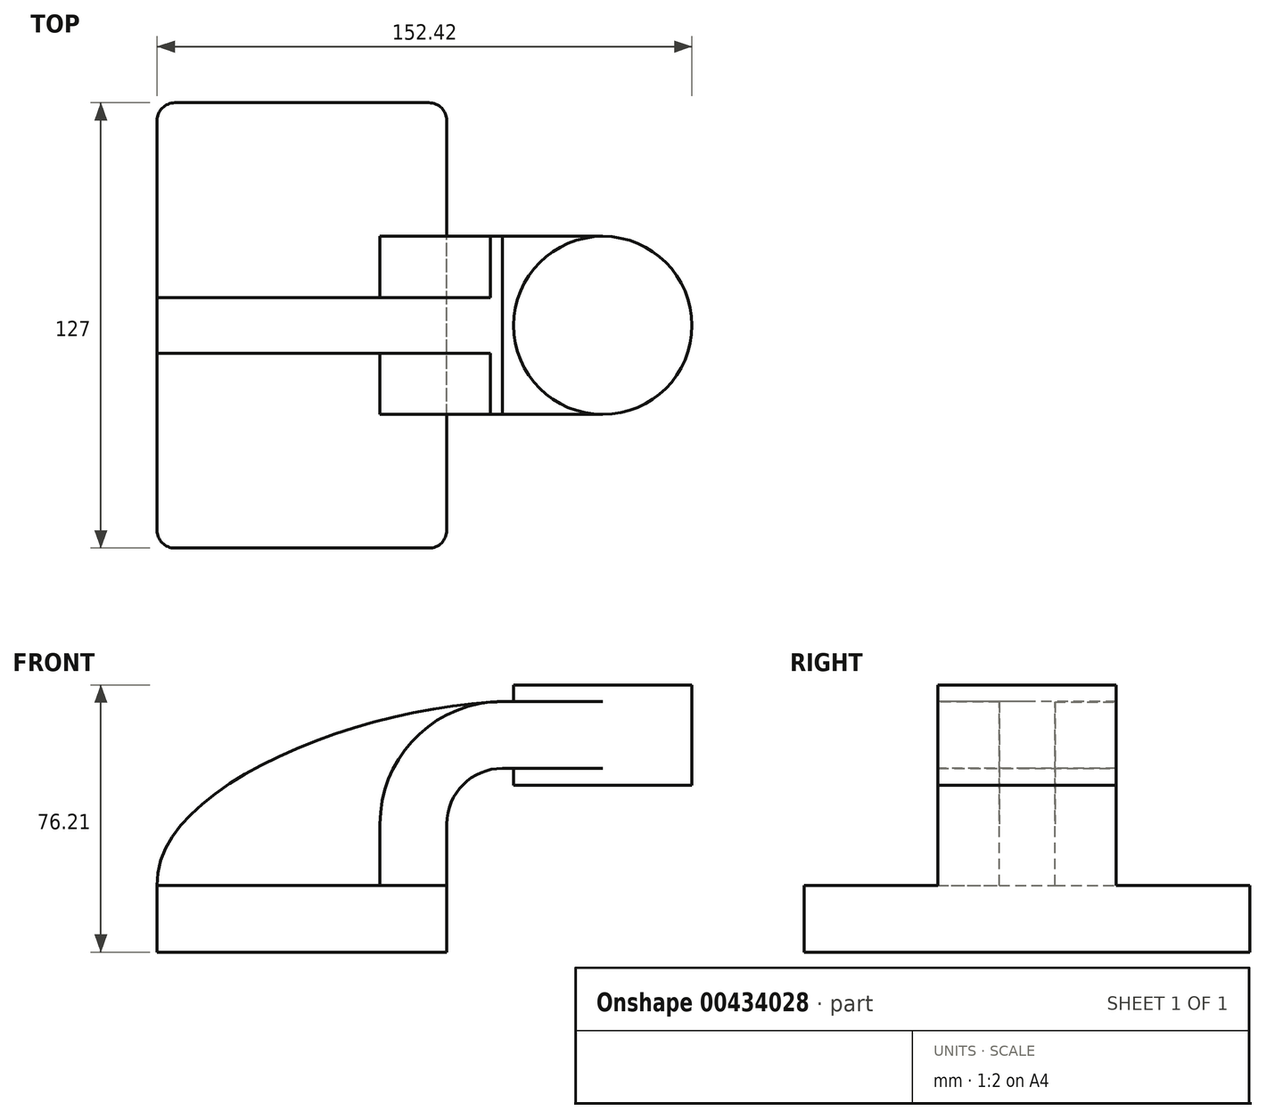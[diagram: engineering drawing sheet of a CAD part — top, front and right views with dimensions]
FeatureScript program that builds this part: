
annotation { "Feature Type Name" : "Feature", "Feature Type Description" : "" }
export const myFeature = defineFeature(function(context is Context, id is Id, definition is map)
    precondition{}
    {
        {
            var Q0;
            Q0=qCreatedBy(makeId("Front.planeOp"),FACE);
            var sketch = newSketch(context, id + "F0", { "sketchPlane" : qUnion([Q0])});
            skLineSegment(sketch, "E0.rect.bottom", {"start": v(-41.28, 9.52) * mm, "end": v(41.28, 9.52) * mm});
            skLineSegment(sketch, "E0.rect.top", {"start": v(-41.28, -9.52) * mm, "end": v(41.28, -9.52) * mm});
            skLineSegment(sketch, "E0.rect.left", {"start": v(-41.28, 9.52) * mm, "end": v(-41.28, -9.52) * mm});
            skLineSegment(sketch, "E0.rect.right", {"start": v(41.28, 9.52) * mm, "end": v(41.28, -9.52) * mm});
            skPoint(sketch, "E0.rect.middle", {"position": v(0, 0) * mm});
            skLineSegment(sketch, "E1", {"start": v(41.28, 9.52) * mm, "end": v(41.28, 27) * mm});
            skArc(sketch, "E2", {"start": v(41.28, 27) * mm, "mid": v(45.92, 38.23) * mm, "end": v(57.15, 42.88) * mm});
            skLineSegment(sketch, "E3", {"start": v(57.15, 42.88) * mm, "end": v(85.72, 42.88) * mm});
            skLineSegment(sketch, "E4.rect.bottom", {"start": v(60.32, 38.1) * mm, "end": v(111.12, 38.1) * mm});
            skLineSegment(sketch, "E4.rect.top", {"start": v(60.32, 66.68) * mm, "end": v(111.12, 66.68) * mm});
            skLineSegment(sketch, "E4.rect.left", {"start": v(60.32, 38.1) * mm, "end": v(60.32, 66.68) * mm});
            skLineSegment(sketch, "E4.rect.right", {"start": v(111.13, 38.1) * mm, "end": v(111.12, 66.68) * mm});
            skPoint(sketch, "E4.rect.middle", {"position": v(85.72, 52.39) * mm});
            skLineSegment(sketch, "E5.0", {"start": v(57.15, 61.93) * mm, "end": v(85.72, 61.93) * mm});
            skArc(sketch, "E5.1", {"start": v(22.23, 27) * mm, "mid": v(32.45, 51.7) * mm, "end": v(57.15, 61.93) * mm});
            skLineSegment(sketch, "E5.2", {"start": v(22.23, 9.52) * mm, "end": v(22.23, 27) * mm});
            skLineSegment(sketch, "E6", {"start": v(85.72, 38.1) * mm, "end": v(85.72, 66.68) * mm});
            skFitSpline(sketch, "E7", {"points": [v(-41.28, 9.52) * mm, v(57.15, 61.93) * mm], "startDerivative": vector(-2.98, 84.8) * mm, "endDerivative": vector(120.92, 4.22) * mm});
            skLineSegment(sketch, "E8", {"start": v(99.43, 120.78) * mm, "end": v(0, 120.78) * mm});
            skLineSegment(sketch, "E9", {"start": v(99.43, 100.25) * mm, "end": v(0, 100.25) * mm});
            skLineSegment(sketch, "E10", {"start": v(99.43, 100.25) * mm, "end": v(99.43, 120.78) * mm, "construction": true});
            skLineSegment(sketch, "E11", {"start": v(0, 120.78) * mm, "end": v(0, 100.25) * mm, "construction": true});
            skSolve(sketch);
        }
        {
            var Q0;
            Q0=makeQuery(id+"F0.imprint","IMPRINT",FACE,{"disambiguationData":[TD([[makeQuery(id+"F0.imprint","IMPRINT",EDGE,{"derivedFrom":sQuery(id+"F0.wireOp",EDGE,"E0.rect.top")}),1.0]])]});
            extrude(context, id + "F1", {"entities" : qUnion([Q0]), "endBound" : BoundingType.SYMMETRIC, "offsetDistance" : 25.4 * mm, "depth" : 127 * mm});
        }
        {
            var Q0;
            {var subQ9=sQuery(id+"F0.wireOp",EDGE,"E1");Q0=makeQuery(id+"F0.imprint","IMPRINT",FACE,{"disambiguationData":[TD([[makeQuery(id+"F0.imprint","IMPRINT",EDGE,{"derivedFrom":subQ9}),1.0]])]});}
            var Q1;
            {var subQ0=sQuery(id+"F0.wireOp",EDGE,"E6");var subQ1=sQuery(id+"F0.wireOp",EDGE,"E3");var subQ2=makeQuery(id+"F0.imprint","INTERSECT",VERTEX,{"derivedFrom":[subQ1,subQ0]});Q1=makeQuery(id+"F0.imprint","IMPRINT",FACE,{"disambiguationData":[TD([[makeQuery(id+"F0.imprint","IMPRINT",EDGE,{"disambiguationData":[TD([[subQ2,1.0]])],"derivedFrom":subQ1}),1.0]])]});}
            extrude(context, id + "F2", {"entities" : qUnion([Q0, Q1]), "operationType" : NewBodyOperationType.ADD, "endBound" : BoundingType.SYMMETRIC, "depth" : 50.8 * mm});
        }
        {
            var Q0;
            {var subQ3=sQuery(id+"F0.wireOp",EDGE,"E5.2");Q0=makeQuery(id+"F0.imprint","IMPRINT",FACE,{"disambiguationData":[TD([[makeQuery(id+"F0.imprint","IMPRINT",EDGE,{"derivedFrom":subQ3}),1.0]])]});}
            extrude(context, id + "F3", {"entities" : qUnion([Q0]), "operationType" : NewBodyOperationType.ADD, "endBound" : BoundingType.SYMMETRIC, "depth" : 15.88 * mm});
        }
        {
            var Q0;
            {var subQ5=sQuery(id+"F0.wireOp",EDGE,"E4.rect.right");Q0=makeQuery(id+"F0.imprint","IMPRINT",FACE,{"disambiguationData":[TD([[makeQuery(id+"F0.imprint","IMPRINT",EDGE,{"derivedFrom":subQ5}),1.0]])]});}
            var Q1;
            Q1=sQuery(id+"F0.wireOp",EDGE,"E6");
            revolve(context, id + "F4", {"operationType" : NewBodyOperationType.ADD, "entities" : qUnion([Q0]), "axis" : qUnion([Q1]), "revolveType" : RevolveType.FULL});
        }
        {
            var Q0;
            Q0=makeQuery(id+"F1.opExtrude","CAP_EDGE",EDGE,{"disambiguationData":[OSD([sQuery(id+"F0.wireOp",EDGE,"E0.rect.right")])],"isStart":false});
            var Q1;
            Q1=makeQuery(id+"F1.opExtrude","CAP_EDGE",EDGE,{"disambiguationData":[OSD([sQuery(id+"F0.wireOp",EDGE,"E0.rect.left")])],"isStart":false});
            var Q2;
            Q2=makeQuery(id+"F1.opExtrude","CAP_EDGE",EDGE,{"disambiguationData":[OSD([sQuery(id+"F0.wireOp",EDGE,"E0.rect.right")])],"isStart":true});
            var Q3;
            Q3=makeQuery(id+"F1.opExtrude","CAP_EDGE",EDGE,{"disambiguationData":[OSD([sQuery(id+"F0.wireOp",EDGE,"E0.rect.left")])],"isStart":true});
            fillet(context, id + "F5", {"entities" : qUnion([Q0, Q1, Q2, Q3]), "radius" : 5.08 * mm, "tangentPropagation" : true, "defaultsChanged" : false, "vertexSettings" : [], "allowEdgeOverflow" : false});
        }
    });
